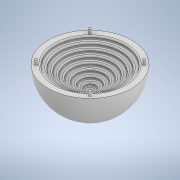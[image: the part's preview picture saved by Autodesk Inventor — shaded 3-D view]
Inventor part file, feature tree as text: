
AUTODESK INVENTOR PART (.ipt)
format: ipt  version: 2022 (Build 260153000, 153)  size: 437,760 bytes
history: native  units: mm
features: extrude x17, sketch x17, other x10, fillet x6
ambient origin geometry x8: Origin, YZ Plane, XZ Plane, XY Plane, X Axis, Y Axis, Z Axis, Center Point
bodies: Body1 (feature_tree)
feature tree (50):
  other  "實體1"
  extrude  "擠出1"  Depth=60.0mm
  fillet  "圓角1"  Radius=30.0mm
  extrude  "擠出2"  Depth=30.0mm
  extrude  "擠出3"  Depth=50.0mm
  extrude  "擠出4"  Depth=2.0mm TaperAngle=0.0deg
  extrude  "擠出5"  Depth=44.0mm
  extrude  "擠出6"  Depth=2.0mm TaperAngle=0.0deg
  extrude  "擠出7"  Depth=38.0mm
  extrude  "擠出8"  Depth=2.0mm TaperAngle=0.0deg
  extrude  "擠出9"  Depth=32.0mm
  extrude  "擠出11"  Depth=2.0mm TaperAngle=0.0deg
  extrude  "擠出12"  Depth=26.0mm
  extrude  "擠出13"  Depth=2.0mm TaperAngle=0.0deg
  extrude  "擠出16"  Depth=20.0mm
  fillet  "圓角2"  Radius=2.0mm
  extrude  "擠出17"  Depth=14.0mm
  fillet  "圓角3"  Radius=2.0mm
  extrude  "擠出18"  Depth=8.0mm
  fillet  "圓角4"  Radius=2.0mm
  extrude  "擠出19"  Depth=3.0mm
  fillet  "圓角5"  Radius=2.0mm
  other  "面圓角1"
  other  "面圓角2"
  other  "面圓角3"
  other  "面圓角4"
  other  "面圓角5"
  other  "面圓角6"
  other  "面圓角7"
  other  "面圓角8"
  extrude  "擠出20"  Depth=3.0mm
  other  "面圓角9"
  fillet  "圓角6"  Radius=50.0mm
  sketch  "草圖3"
  sketch  "草圖4"
  sketch  "草圖5"
  sketch  "草圖6"
  sketch  "草圖7"
  sketch  "草圖8"
  sketch  "草圖9"
  sketch  "草圖10"
  sketch  "草圖11"
  sketch  "草圖14"
  sketch  "草圖15"
  sketch  "草圖16"
  sketch  "草圖25"
  sketch  "草圖26"
  sketch  "草圖27"
  sketch  "草圖29"
  sketch  "草圖30"
